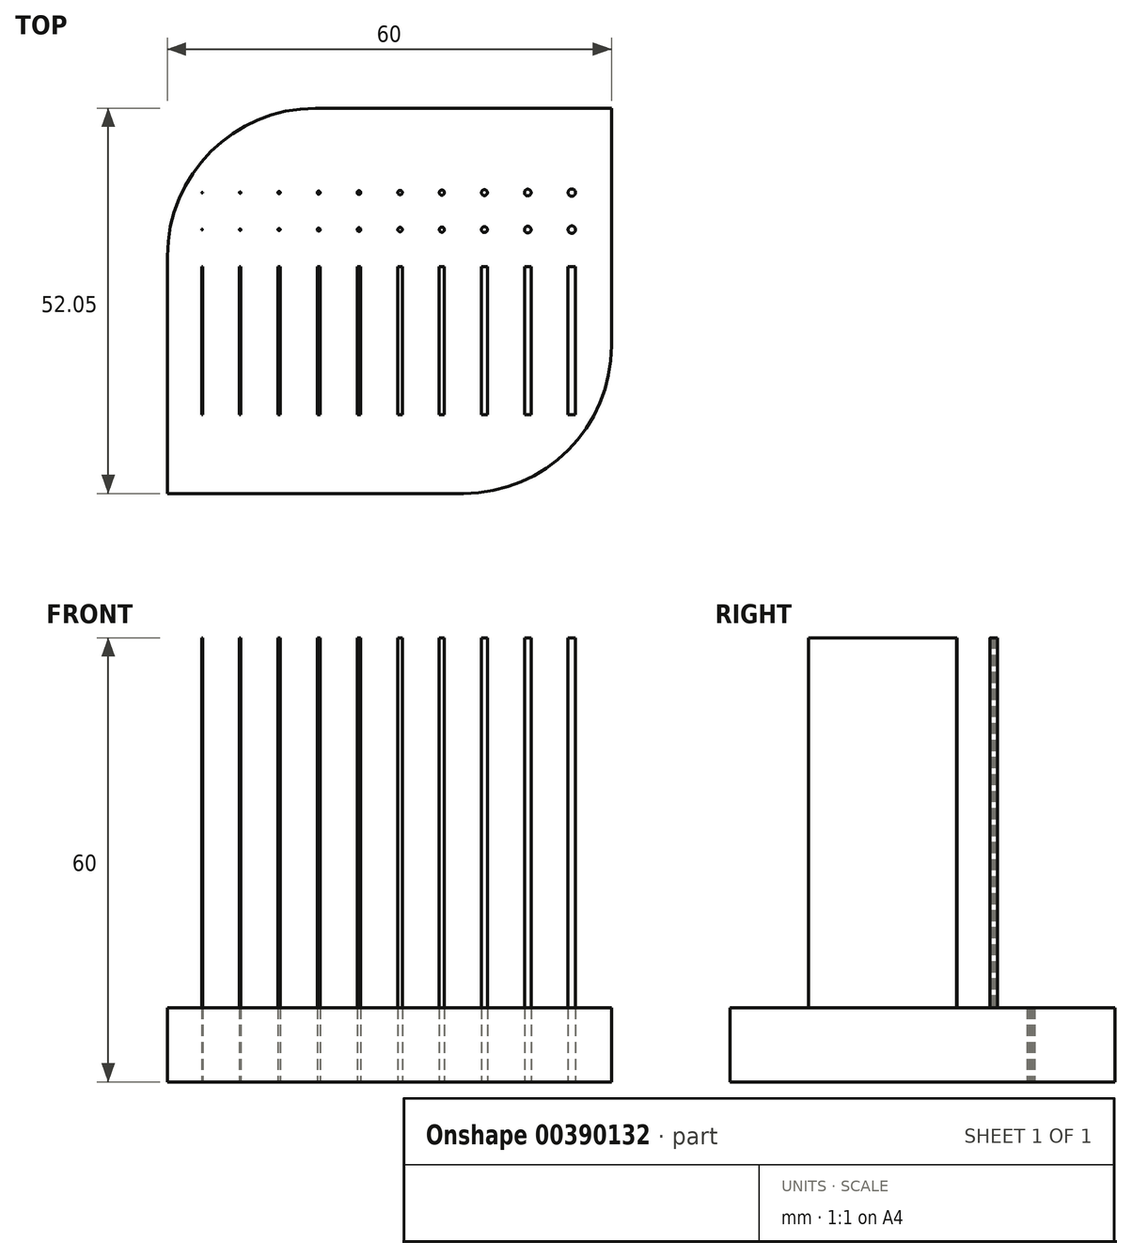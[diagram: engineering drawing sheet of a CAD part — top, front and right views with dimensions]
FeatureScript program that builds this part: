
annotation { "Feature Type Name" : "Feature", "Feature Type Description" : "" }
export const myFeature = defineFeature(function(context is Context, id is Id, definition is map)
    precondition{}
    {
        {
            var Q0;
            Q0=qCreatedBy(makeId("Top.planeOp"),FACE);
            var sketch = newSketch(context, id + "F0", { "sketchPlane" : qUnion([Q0])});
            skLineSegment(sketch, "E0.bottom", {"start": v(-10, 29.74) * mm, "end": v(30, 29.74) * mm});
            skLineSegment(sketch, "E0.top", {"start": v(-30, -22.3) * mm, "end": v(10, -22.3) * mm});
            skLineSegment(sketch, "E0.left", {"start": v(-30, 9.74) * mm, "end": v(-30, -22.3) * mm});
            skLineSegment(sketch, "E0.right", {"start": v(30, 29.74) * mm, "end": v(30, -2.3) * mm});
            skPoint(sketch, "E1.visualSharp", {"position": v(-30, 29.74) * mm});
            skArc(sketch, "E1.filletArc", {"start": v(-10, 29.74) * mm, "mid": v(-24.14, 23.88) * mm, "end": v(-30, 9.74) * mm});
            skPoint(sketch, "E2.visualSharp", {"position": v(30, -22.3) * mm});
            skArc(sketch, "E2.filletArc", {"start": v(10, -22.3) * mm, "mid": v(24.14, -16.45) * mm, "end": v(30, -2.3) * mm});
            skLineSegment(sketch, "E3.bottom", {"start": v(-25.37, 8.34) * mm, "end": v(-25.27, 8.34) * mm});
            skLineSegment(sketch, "E3.top", {"start": v(-25.37, -11.67) * mm, "end": v(-25.27, -11.67) * mm});
            skLineSegment(sketch, "E3.left", {"start": v(-25.37, 8.34) * mm, "end": v(-25.37, -11.67) * mm});
            skLineSegment(sketch, "E3.right", {"start": v(-25.27, 8.34) * mm, "end": v(-25.27, -11.67) * mm});
            skLineSegment(sketch, "E4.bottom", {"start": v(-20.27, 8.33) * mm, "end": v(-20.07, 8.33) * mm});
            skLineSegment(sketch, "E4.top", {"start": v(-20.27, -11.67) * mm, "end": v(-20.07, -11.67) * mm});
            skLineSegment(sketch, "E4.left", {"start": v(-20.27, 8.33) * mm, "end": v(-20.27, -11.67) * mm});
            skLineSegment(sketch, "E4.right", {"start": v(-20.07, 8.33) * mm, "end": v(-20.07, -11.67) * mm});
            skLineSegment(sketch, "E5.bottom", {"start": v(-15.07, 8.33) * mm, "end": v(-14.77, 8.33) * mm});
            skLineSegment(sketch, "E5.top", {"start": v(-15.07, -11.67) * mm, "end": v(-14.77, -11.67) * mm});
            skLineSegment(sketch, "E5.left", {"start": v(-15.07, 8.33) * mm, "end": v(-15.07, -11.67) * mm});
            skLineSegment(sketch, "E5.right", {"start": v(-14.77, 8.33) * mm, "end": v(-14.77, -11.67) * mm});
            skLineSegment(sketch, "E6.bottom", {"start": v(-9.77, 8.33) * mm, "end": v(-9.37, 8.33) * mm});
            skLineSegment(sketch, "E6.top", {"start": v(-9.77, -11.67) * mm, "end": v(-9.37, -11.67) * mm});
            skLineSegment(sketch, "E6.left", {"start": v(-9.77, 8.33) * mm, "end": v(-9.77, -11.67) * mm});
            skLineSegment(sketch, "E6.right", {"start": v(-9.37, 8.33) * mm, "end": v(-9.37, -11.67) * mm});
            skLineSegment(sketch, "E7.bottom", {"start": v(-4.37, 8.33) * mm, "end": v(-3.87, 8.33) * mm});
            skLineSegment(sketch, "E7.top", {"start": v(-4.37, -11.67) * mm, "end": v(-3.87, -11.67) * mm});
            skLineSegment(sketch, "E7.left", {"start": v(-4.37, 8.33) * mm, "end": v(-4.37, -11.67) * mm});
            skLineSegment(sketch, "E7.right", {"start": v(-3.87, 8.33) * mm, "end": v(-3.87, -11.67) * mm});
            skLineSegment(sketch, "E8.bottom", {"start": v(1.13, 8.33) * mm, "end": v(1.73, 8.33) * mm});
            skLineSegment(sketch, "E8.top", {"start": v(1.13, -11.67) * mm, "end": v(1.73, -11.67) * mm});
            skLineSegment(sketch, "E8.left", {"start": v(1.13, 8.33) * mm, "end": v(1.13, -11.67) * mm});
            skLineSegment(sketch, "E8.right", {"start": v(1.73, 8.33) * mm, "end": v(1.73, -11.67) * mm});
            skLineSegment(sketch, "E9.bottom", {"start": v(7.43, 8.33) * mm, "end": v(6.73, 8.33) * mm});
            skLineSegment(sketch, "E9.top", {"start": v(7.43, -11.67) * mm, "end": v(6.73, -11.67) * mm});
            skLineSegment(sketch, "E9.left", {"start": v(7.43, 8.33) * mm, "end": v(7.43, -11.67) * mm});
            skLineSegment(sketch, "E9.right", {"start": v(6.73, 8.33) * mm, "end": v(6.73, -11.67) * mm});
            skLineSegment(sketch, "E10.bottom", {"start": v(13.23, 8.33) * mm, "end": v(12.43, 8.33) * mm});
            skLineSegment(sketch, "E10.top", {"start": v(13.23, -11.67) * mm, "end": v(12.43, -11.67) * mm});
            skLineSegment(sketch, "E10.left", {"start": v(13.23, 8.33) * mm, "end": v(13.23, -11.67) * mm});
            skLineSegment(sketch, "E10.right", {"start": v(12.43, 8.33) * mm, "end": v(12.43, -11.67) * mm});
            skPoint(sketch, "E11.oppositeSnap0", {"position": v(12.83, -11.67) * mm});
            skLineSegment(sketch, "E11.bottom", {"start": v(19.13, 8.33) * mm, "end": v(18.23, 8.33) * mm});
            skLineSegment(sketch, "E11.top", {"start": v(19.13, -11.67) * mm, "end": v(18.23, -11.67) * mm});
            skLineSegment(sketch, "E11.left", {"start": v(19.13, 8.33) * mm, "end": v(19.13, -11.67) * mm});
            skLineSegment(sketch, "E11.right", {"start": v(18.23, 8.33) * mm, "end": v(18.23, -11.67) * mm});
            skLineSegment(sketch, "E12.bottom", {"start": v(24.13, 8.33) * mm, "end": v(25.13, 8.33) * mm});
            skLineSegment(sketch, "E12.top", {"start": v(24.13, -11.67) * mm, "end": v(25.13, -11.67) * mm});
            skLineSegment(sketch, "E12.left", {"start": v(24.13, 8.33) * mm, "end": v(24.13, -11.67) * mm});
            skLineSegment(sketch, "E12.right", {"start": v(25.13, 8.33) * mm, "end": v(25.13, -11.67) * mm});
            skLineSegment(sketch, "E13", {"start": v(-25.37, -11.67) * mm, "end": v(25.13, -11.67) * mm, "construction": true});
            skCircle(sketch, "E14", {"center": v(-25.32, 13.34) * mm, "radius": 0.05 * mm});
            skCircle(sketch, "E15", {"center": v(-20.17, 13.34) * mm, "radius": 0.1 * mm});
            skCircle(sketch, "E16", {"center": v(-14.92, 13.34) * mm, "radius": 0.15 * mm});
            skCircle(sketch, "E17", {"center": v(-9.57, 13.34) * mm, "radius": 0.2 * mm});
            skCircle(sketch, "E18", {"center": v(-4.12, 13.34) * mm, "radius": 0.25 * mm});
            skCircle(sketch, "E19", {"center": v(1.43, 13.34) * mm, "radius": 0.3 * mm});
            skCircle(sketch, "E20", {"center": v(7.08, 13.34) * mm, "radius": 0.35 * mm});
            skCircle(sketch, "E21", {"center": v(12.83, 13.34) * mm, "radius": 0.4 * mm});
            skCircle(sketch, "E22", {"center": v(18.68, 13.34) * mm, "radius": 0.45 * mm});
            skCircle(sketch, "E23", {"center": v(24.63, 13.34) * mm, "radius": 0.5 * mm});
            skLineSegment(sketch, "E24", {"start": v(24.63, 8.33) * mm, "end": v(24.63, 13.34) * mm, "construction": true});
            skLineSegment(sketch, "E25", {"start": v(24.63, 13.34) * mm, "end": v(-25.32, 13.34) * mm, "construction": true});
            skPoint(sketch, "E25.endSnap0", {"position": v(-25.32, 8.34) * mm});
            skLineSegment(sketch, "E26", {"start": v(-25.32, 8.34) * mm, "end": v(-25.32, 13.34) * mm, "construction": true});
            skLineSegment(sketch, "E27", {"start": v(-20.17, 8.33) * mm, "end": v(-20.17, 13.34) * mm, "construction": true});
            skLineSegment(sketch, "E28", {"start": v(-14.92, 8.33) * mm, "end": v(-14.92, 13.34) * mm, "construction": true});
            skLineSegment(sketch, "E29", {"start": v(-9.57, 8.33) * mm, "end": v(-9.57, 13.34) * mm, "construction": true});
            skLineSegment(sketch, "E30", {"start": v(-4.12, 8.33) * mm, "end": v(-4.12, 13.34) * mm, "construction": true});
            skLineSegment(sketch, "E31", {"start": v(1.43, 8.33) * mm, "end": v(1.43, 13.34) * mm, "construction": true});
            skLineSegment(sketch, "E32", {"start": v(7.08, 8.33) * mm, "end": v(7.08, 13.34) * mm, "construction": true});
            skLineSegment(sketch, "E33", {"start": v(12.83, 8.33) * mm, "end": v(12.83, 13.34) * mm, "construction": true});
            skLineSegment(sketch, "E34", {"start": v(18.68, 8.33) * mm, "end": v(18.68, 13.34) * mm, "construction": true});
            skCircle(sketch, "E35", {"center": v(-25.3, 18.34) * mm, "radius": 0.05 * mm});
            skCircle(sketch, "E36", {"center": v(-20.17, 18.34) * mm, "radius": 0.1 * mm});
            skCircle(sketch, "E37", {"center": v(-14.92, 18.34) * mm, "radius": 0.15 * mm});
            skCircle(sketch, "E38", {"center": v(-9.57, 18.34) * mm, "radius": 0.2 * mm});
            skCircle(sketch, "E39", {"center": v(-4.12, 18.34) * mm, "radius": 0.25 * mm});
            skCircle(sketch, "E40", {"center": v(1.43, 18.34) * mm, "radius": 0.3 * mm});
            skCircle(sketch, "E41", {"center": v(7.08, 18.34) * mm, "radius": 0.35 * mm});
            skCircle(sketch, "E42", {"center": v(12.83, 18.34) * mm, "radius": 0.4 * mm});
            skCircle(sketch, "E43", {"center": v(18.68, 18.34) * mm, "radius": 0.45 * mm});
            skCircle(sketch, "E44", {"center": v(24.63, 18.34) * mm, "radius": 0.5 * mm});
            skLineSegment(sketch, "E45", {"start": v(24.63, 18.34) * mm, "end": v(-25.3, 18.34) * mm, "construction": true});
            skLineSegment(sketch, "E46", {"start": v(-25.32, 13.34) * mm, "end": v(-25.3, 18.34) * mm, "construction": true});
            skLineSegment(sketch, "E47", {"start": v(-20.17, 13.34) * mm, "end": v(-20.17, 18.34) * mm, "construction": true});
            skLineSegment(sketch, "E48", {"start": v(-14.92, 13.34) * mm, "end": v(-14.92, 18.34) * mm, "construction": true});
            skLineSegment(sketch, "E49", {"start": v(-9.57, 13.34) * mm, "end": v(-9.57, 18.34) * mm, "construction": true});
            skLineSegment(sketch, "E50", {"start": v(-4.12, 13.34) * mm, "end": v(-4.12, 18.34) * mm, "construction": true});
            skLineSegment(sketch, "E51", {"start": v(1.43, 13.34) * mm, "end": v(1.43, 18.34) * mm, "construction": true});
            skLineSegment(sketch, "E52", {"start": v(7.08, 13.34) * mm, "end": v(7.08, 18.34) * mm, "construction": true});
            skLineSegment(sketch, "E53", {"start": v(12.83, 13.34) * mm, "end": v(12.83, 18.34) * mm, "construction": true});
            skLineSegment(sketch, "E54", {"start": v(18.68, 13.34) * mm, "end": v(18.68, 18.34) * mm, "construction": true});
            skLineSegment(sketch, "E55", {"start": v(24.63, 13.34) * mm, "end": v(24.63, 18.34) * mm, "construction": true});
            skSolve(sketch);
        }
        {
            var Q0;
            Q0=makeQuery(id+"F0.imprint","IMPRINT",FACE,{"disambiguationData":[TD([[makeQuery(id+"F0.imprint","IMPRINT",EDGE,{"derivedFrom":sQuery(id+"F0.wireOp",EDGE,"E10.bottom")}),1.0]])]});
            var Q1;
            Q1=makeQuery(id+"F0.imprint","IMPRINT",FACE,{"disambiguationData":[TD([[makeQuery(id+"F0.imprint","IMPRINT",EDGE,{"derivedFrom":sQuery(id+"F0.wireOp",EDGE,"E11.bottom")}),1.0]])]});
            var Q2;
            Q2=makeQuery(id+"F0.imprint","IMPRINT",FACE,{"disambiguationData":[TD([[makeQuery(id+"F0.imprint","IMPRINT",EDGE,{"derivedFrom":sQuery(id+"F0.wireOp",EDGE,"E12.bottom")}),-1.0]])]});
            var Q3;
            Q3=makeQuery(id+"F0.imprint","IMPRINT",FACE,{"disambiguationData":[TD([[makeQuery(id+"F0.imprint","IMPRINT",EDGE,{"derivedFrom":sQuery(id+"F0.wireOp",EDGE,"E3.bottom")}),-1.0]])]});
            var Q4;
            Q4=makeQuery(id+"F0.imprint","IMPRINT",FACE,{"disambiguationData":[TD([[makeQuery(id+"F0.imprint","IMPRINT",EDGE,{"derivedFrom":sQuery(id+"F0.wireOp",EDGE,"E4.bottom")}),-1.0]])]});
            var Q5;
            Q5=makeQuery(id+"F0.imprint","IMPRINT",FACE,{"disambiguationData":[TD([[makeQuery(id+"F0.imprint","IMPRINT",EDGE,{"derivedFrom":sQuery(id+"F0.wireOp",EDGE,"E5.bottom")}),-1.0]])]});
            var Q6;
            Q6=makeQuery(id+"F0.imprint","IMPRINT",FACE,{"disambiguationData":[TD([[makeQuery(id+"F0.imprint","IMPRINT",EDGE,{"derivedFrom":sQuery(id+"F0.wireOp",EDGE,"E6.bottom")}),-1.0]])]});
            var Q7;
            Q7=makeQuery(id+"F0.imprint","IMPRINT",FACE,{"disambiguationData":[TD([[makeQuery(id+"F0.imprint","IMPRINT",EDGE,{"derivedFrom":sQuery(id+"F0.wireOp",EDGE,"E7.bottom")}),-1.0]])]});
            var Q8;
            Q8=makeQuery(id+"F0.imprint","IMPRINT",FACE,{"disambiguationData":[TD([[makeQuery(id+"F0.imprint","IMPRINT",EDGE,{"derivedFrom":sQuery(id+"F0.wireOp",EDGE,"E8.bottom")}),-1.0]])]});
            var Q9;
            Q9=makeQuery(id+"F0.imprint","IMPRINT",FACE,{"disambiguationData":[TD([[makeQuery(id+"F0.imprint","IMPRINT",EDGE,{"derivedFrom":sQuery(id+"F0.wireOp",EDGE,"E9.bottom")}),1.0]])]});
            var Q10;
            Q10=makeQuery(id+"F0.imprint","IMPRINT",FACE,{"disambiguationData":[TD([[makeQuery(id+"F0.imprint","IMPRINT",EDGE,{"derivedFrom":sQuery(id+"F0.wireOp",EDGE,"E19")}),1.0]])]});
            var Q11;
            Q11=makeQuery(id+"F0.imprint","IMPRINT",FACE,{"disambiguationData":[TD([[makeQuery(id+"F0.imprint","IMPRINT",EDGE,{"derivedFrom":sQuery(id+"F0.wireOp",EDGE,"E17")}),1.0]])]});
            var Q12;
            Q12=makeQuery(id+"F0.imprint","IMPRINT",FACE,{"disambiguationData":[TD([[makeQuery(id+"F0.imprint","IMPRINT",EDGE,{"derivedFrom":sQuery(id+"F0.wireOp",EDGE,"E18")}),1.0]])]});
            var Q13;
            Q13=makeQuery(id+"F0.imprint","IMPRINT",FACE,{"disambiguationData":[TD([[makeQuery(id+"F0.imprint","IMPRINT",EDGE,{"derivedFrom":sQuery(id+"F0.wireOp",EDGE,"E20")}),1.0]])]});
            var Q14;
            Q14=makeQuery(id+"F0.imprint","IMPRINT",FACE,{"disambiguationData":[TD([[makeQuery(id+"F0.imprint","IMPRINT",EDGE,{"derivedFrom":sQuery(id+"F0.wireOp",EDGE,"E15")}),1.0]])]});
            var Q15;
            Q15=makeQuery(id+"F0.imprint","IMPRINT",FACE,{"disambiguationData":[TD([[makeQuery(id+"F0.imprint","IMPRINT",EDGE,{"derivedFrom":sQuery(id+"F0.wireOp",EDGE,"E16")}),1.0]])]});
            var Q16;
            Q16=makeQuery(id+"F0.imprint","IMPRINT",FACE,{"disambiguationData":[TD([[makeQuery(id+"F0.imprint","IMPRINT",EDGE,{"derivedFrom":sQuery(id+"F0.wireOp",EDGE,"E21")}),1.0]])]});
            var Q17;
            Q17=makeQuery(id+"F0.imprint","IMPRINT",FACE,{"disambiguationData":[TD([[makeQuery(id+"F0.imprint","IMPRINT",EDGE,{"derivedFrom":sQuery(id+"F0.wireOp",EDGE,"E22")}),1.0]])]});
            var Q18;
            Q18=makeQuery(id+"F0.imprint","IMPRINT",FACE,{"disambiguationData":[TD([[makeQuery(id+"F0.imprint","IMPRINT",EDGE,{"derivedFrom":sQuery(id+"F0.wireOp",EDGE,"E23")}),1.0]])]});
            var Q19;
            Q19=makeQuery(id+"F0.imprint","IMPRINT",FACE,{"disambiguationData":[TD([[makeQuery(id+"F0.imprint","IMPRINT",EDGE,{"derivedFrom":sQuery(id+"F0.wireOp",EDGE,"E14")}),1.0]])]});
            var Q20;
            Q20=makeQuery(id+"F0.imprint","IMPRINT",FACE,{"disambiguationData":[TD([[makeQuery(id+"F0.imprint","IMPRINT",EDGE,{"derivedFrom":sQuery(id+"F0.wireOp",EDGE,"E0.bottom")}),-1.0]])]});
            extrude(context, id + "F1", {"entities" : qUnion([Q0, Q1, Q2, Q3, Q4, Q5, Q6, Q7, Q8, Q9, Q10, Q11, Q12, Q13, Q14, Q15, Q16, Q17, Q18, Q19, Q20]), "depth" : 10 * mm});
        }
        {
            var Q0;
            Q0=makeQuery(id+"F1.opExtrude","CAP_FACE",FACE,{"disambiguationData":[OSD([sQuery(id+"F0.wireOp",EDGE,"E0.bottom"),sQuery(id+"F0.wireOp",EDGE,"E0.top"),sQuery(id+"F0.wireOp",EDGE,"E0.left"),sQuery(id+"F0.wireOp",EDGE,"E0.right"),sQuery(id+"F0.wireOp",EDGE,"E1.filletArc"),sQuery(id+"F0.wireOp",EDGE,"E2.filletArc"),sQuery(id+"F0.wireOp",EDGE,"E35"),sQuery(id+"F0.wireOp",EDGE,"E36"),sQuery(id+"F0.wireOp",EDGE,"E37"),sQuery(id+"F0.wireOp",EDGE,"E38"),sQuery(id+"F0.wireOp",EDGE,"E39"),sQuery(id+"F0.wireOp",EDGE,"E40"),sQuery(id+"F0.wireOp",EDGE,"E41"),sQuery(id+"F0.wireOp",EDGE,"E42"),sQuery(id+"F0.wireOp",EDGE,"E43"),sQuery(id+"F0.wireOp",EDGE,"E44")])],"isStart":false});
            var sketch = newSketch(context, id + "F2", { "sketchPlane" : qUnion([Q0])});
            skLineSegment(sketch, "E56.0", {"start": v(18.23, 8.33) * mm, "end": v(18.23, -11.67) * mm});
            skLineSegment(sketch, "E56.2", {"start": v(6.73, 8.33) * mm, "end": v(6.73, -11.67) * mm});
            skLineSegment(sketch, "E56.4", {"start": v(-14.77, 8.33) * mm, "end": v(-14.77, -11.67) * mm});
            skLineSegment(sketch, "E56.5", {"start": v(7.43, 8.33) * mm, "end": v(7.43, -11.67) * mm});
            skLineSegment(sketch, "E56.6", {"start": v(-3.87, 8.33) * mm, "end": v(-3.87, -11.67) * mm});
            skLineSegment(sketch, "E56.9", {"start": v(19.13, 8.33) * mm, "end": v(19.13, -11.67) * mm});
            skLineSegment(sketch, "E56.10", {"start": v(-4.37, 8.33) * mm, "end": v(-4.37, -11.67) * mm});
            skLineSegment(sketch, "E56.11", {"start": v(-15.07, 8.33) * mm, "end": v(-15.07, -11.67) * mm});
            skLineSegment(sketch, "E56.12", {"start": v(-20.27, 8.33) * mm, "end": v(-20.27, -11.67) * mm});
            skLineSegment(sketch, "E56.13", {"start": v(-25.27, 8.34) * mm, "end": v(-25.27, -11.67) * mm});
            skLineSegment(sketch, "E56.14", {"start": v(-25.37, 8.34) * mm, "end": v(-25.37, -11.67) * mm});
            skLineSegment(sketch, "E56.15", {"start": v(-20.07, 8.33) * mm, "end": v(-20.07, -11.67) * mm});
            skLineSegment(sketch, "E56.17", {"start": v(12.43, 8.33) * mm, "end": v(12.43, -11.67) * mm});
            skLineSegment(sketch, "E56.20", {"start": v(-9.37, 8.33) * mm, "end": v(-9.37, -11.67) * mm});
            skLineSegment(sketch, "E56.21", {"start": v(1.13, 8.33) * mm, "end": v(1.13, -11.67) * mm});
            skLineSegment(sketch, "E56.23", {"start": v(24.13, 8.33) * mm, "end": v(24.13, -11.67) * mm});
            skLineSegment(sketch, "E56.24", {"start": v(1.73, 8.33) * mm, "end": v(1.73, -11.67) * mm});
            skLineSegment(sketch, "E56.25", {"start": v(13.23, 8.33) * mm, "end": v(13.23, -11.67) * mm});
            skLineSegment(sketch, "E56.26", {"start": v(25.13, 8.33) * mm, "end": v(25.13, -11.67) * mm});
            skLineSegment(sketch, "E56.28", {"start": v(-9.77, 8.33) * mm, "end": v(-9.77, -11.67) * mm});
            skCircle(sketch, "E56.32", {"center": v(-20.17, 13.34) * mm, "radius": 0.1 * mm});
            skCircle(sketch, "E56.33", {"center": v(-14.92, 13.34) * mm, "radius": 0.15 * mm});
            skCircle(sketch, "E56.34", {"center": v(24.63, 13.34) * mm, "radius": 0.5 * mm});
            skCircle(sketch, "E56.35", {"center": v(18.68, 13.34) * mm, "radius": 0.45 * mm});
            skCircle(sketch, "E56.36", {"center": v(1.43, 13.34) * mm, "radius": 0.3 * mm});
            skCircle(sketch, "E56.37", {"center": v(-9.57, 13.34) * mm, "radius": 0.2 * mm});
            skCircle(sketch, "E56.38", {"center": v(-25.32, 13.34) * mm, "radius": 0.05 * mm});
            skCircle(sketch, "E56.39", {"center": v(12.83, 13.34) * mm, "radius": 0.4 * mm});
            skCircle(sketch, "E56.40", {"center": v(7.08, 13.34) * mm, "radius": 0.35 * mm});
            skCircle(sketch, "E56.41", {"center": v(-4.12, 13.34) * mm, "radius": 0.25 * mm});
            skLineSegment(sketch, "E57.0", {"start": v(24.13, 8.33) * mm, "end": v(25.13, 8.33) * mm});
            skLineSegment(sketch, "E58.0", {"start": v(19.13, 8.33) * mm, "end": v(18.23, 8.33) * mm});
            skLineSegment(sketch, "E59.0", {"start": v(13.23, 8.33) * mm, "end": v(12.43, 8.33) * mm});
            skLineSegment(sketch, "E60.0", {"start": v(7.43, 8.33) * mm, "end": v(6.73, 8.33) * mm});
            skLineSegment(sketch, "E61.0", {"start": v(1.13, 8.33) * mm, "end": v(1.73, 8.33) * mm});
            skLineSegment(sketch, "E62.0", {"start": v(-4.37, 8.33) * mm, "end": v(-3.87, 8.33) * mm});
            skLineSegment(sketch, "E63.0", {"start": v(-9.77, 8.33) * mm, "end": v(-9.37, 8.33) * mm});
            skLineSegment(sketch, "E64.0", {"start": v(-15.07, 8.33) * mm, "end": v(-14.77, 8.33) * mm});
            skLineSegment(sketch, "E65.0", {"start": v(-20.27, 8.33) * mm, "end": v(-20.07, 8.33) * mm});
            skLineSegment(sketch, "E66.0", {"start": v(-25.37, 8.34) * mm, "end": v(-25.27, 8.34) * mm});
            skLineSegment(sketch, "E67.0", {"start": v(-20.27, -11.67) * mm, "end": v(-20.07, -11.67) * mm});
            skLineSegment(sketch, "E68", {"start": v(-15.07, -11.67) * mm, "end": v(-14.77, -11.67) * mm});
            skLineSegment(sketch, "E69", {"start": v(-9.77, -11.67) * mm, "end": v(-9.37, -11.67) * mm});
            skLineSegment(sketch, "E70", {"start": v(-4.37, -11.67) * mm, "end": v(-3.87, -11.67) * mm});
            skLineSegment(sketch, "E71", {"start": v(1.13, -11.67) * mm, "end": v(1.73, -11.67) * mm});
            skLineSegment(sketch, "E72", {"start": v(6.73, -11.67) * mm, "end": v(7.43, -11.67) * mm});
            skLineSegment(sketch, "E73", {"start": v(12.43, -11.67) * mm, "end": v(13.23, -11.67) * mm});
            skLineSegment(sketch, "E74", {"start": v(18.23, -11.67) * mm, "end": v(19.13, -11.67) * mm});
            skLineSegment(sketch, "E75", {"start": v(24.13, -11.67) * mm, "end": v(25.13, -11.67) * mm});
            skLineSegment(sketch, "E76", {"start": v(-25.37, -11.67) * mm, "end": v(-25.27, -11.67) * mm});
            skSolve(sketch);
        }
        {
            var Q0;
            Q0=makeQuery(id+"F2.imprint","IMPRINT",FACE,{"disambiguationData":[TD([[makeQuery(id+"F2.imprint","IMPRINT",EDGE,{"derivedFrom":sQuery(id+"F2.wireOp",EDGE,"E56.23")}),1.0]])]});
            var Q1;
            Q1=makeQuery(id+"F2.imprint","IMPRINT",FACE,{"disambiguationData":[TD([[makeQuery(id+"F2.imprint","IMPRINT",EDGE,{"derivedFrom":sQuery(id+"F2.wireOp",EDGE,"E56.12")}),1.0]])]});
            var Q2;
            Q2=makeQuery(id+"F2.imprint","IMPRINT",FACE,{"disambiguationData":[TD([[makeQuery(id+"F2.imprint","IMPRINT",EDGE,{"derivedFrom":sQuery(id+"F2.wireOp",EDGE,"E56.6")}),-1.0]])]});
            var Q3;
            Q3=makeQuery(id+"F2.imprint","IMPRINT",FACE,{"disambiguationData":[TD([[makeQuery(id+"F2.imprint","IMPRINT",EDGE,{"derivedFrom":sQuery(id+"F2.wireOp",EDGE,"E56.0")}),1.0]])]});
            var Q4;
            Q4=makeQuery(id+"F2.imprint","IMPRINT",FACE,{"disambiguationData":[TD([[makeQuery(id+"F2.imprint","IMPRINT",EDGE,{"derivedFrom":sQuery(id+"F2.wireOp",EDGE,"E56.2")}),1.0]])]});
            var Q5;
            Q5=makeQuery(id+"F2.imprint","IMPRINT",FACE,{"disambiguationData":[TD([[makeQuery(id+"F2.imprint","IMPRINT",EDGE,{"derivedFrom":sQuery(id+"F2.wireOp",EDGE,"E56.17")}),1.0]])]});
            var Q6;
            Q6=makeQuery(id+"F2.imprint","IMPRINT",FACE,{"disambiguationData":[TD([[makeQuery(id+"F2.imprint","IMPRINT",EDGE,{"derivedFrom":sQuery(id+"F2.wireOp",EDGE,"E56.21")}),1.0]])]});
            var Q7;
            Q7=makeQuery(id+"F2.imprint","IMPRINT",FACE,{"disambiguationData":[TD([[makeQuery(id+"F2.imprint","IMPRINT",EDGE,{"derivedFrom":sQuery(id+"F2.wireOp",EDGE,"E56.40")}),1.0]])]});
            var Q8;
            Q8=makeQuery(id+"F2.imprint","IMPRINT",FACE,{"disambiguationData":[TD([[makeQuery(id+"F2.imprint","IMPRINT",EDGE,{"derivedFrom":sQuery(id+"F2.wireOp",EDGE,"E56.37")}),1.0]])]});
            var Q9;
            Q9=makeQuery(id+"F2.imprint","IMPRINT",FACE,{"disambiguationData":[TD([[makeQuery(id+"F2.imprint","IMPRINT",EDGE,{"derivedFrom":sQuery(id+"F2.wireOp",EDGE,"E56.33")}),1.0]])]});
            var Q10;
            Q10=makeQuery(id+"F2.imprint","IMPRINT",FACE,{"disambiguationData":[TD([[makeQuery(id+"F2.imprint","IMPRINT",EDGE,{"derivedFrom":sQuery(id+"F2.wireOp",EDGE,"E56.32")}),1.0]])]});
            var Q11;
            Q11=makeQuery(id+"F2.imprint","IMPRINT",FACE,{"disambiguationData":[TD([[makeQuery(id+"F2.imprint","IMPRINT",EDGE,{"derivedFrom":sQuery(id+"F2.wireOp",EDGE,"E56.4")}),-1.0]])]});
            var Q12;
            Q12=makeQuery(id+"F2.imprint","IMPRINT",FACE,{"disambiguationData":[TD([[makeQuery(id+"F2.imprint","IMPRINT",EDGE,{"derivedFrom":sQuery(id+"F2.wireOp",EDGE,"E56.36")}),1.0]])]});
            var Q13;
            Q13=makeQuery(id+"F2.imprint","IMPRINT",FACE,{"disambiguationData":[TD([[makeQuery(id+"F2.imprint","IMPRINT",EDGE,{"derivedFrom":sQuery(id+"F2.wireOp",EDGE,"E56.39")}),1.0]])]});
            var Q14;
            Q14=makeQuery(id+"F2.imprint","IMPRINT",FACE,{"disambiguationData":[TD([[makeQuery(id+"F2.imprint","IMPRINT",EDGE,{"derivedFrom":sQuery(id+"F2.wireOp",EDGE,"E56.38")}),1.0]])]});
            var Q15;
            Q15=makeQuery(id+"F2.imprint","IMPRINT",FACE,{"disambiguationData":[TD([[makeQuery(id+"F2.imprint","IMPRINT",EDGE,{"derivedFrom":sQuery(id+"F2.wireOp",EDGE,"E56.35")}),1.0]])]});
            var Q16;
            Q16=makeQuery(id+"F2.imprint","IMPRINT",FACE,{"disambiguationData":[TD([[makeQuery(id+"F2.imprint","IMPRINT",EDGE,{"derivedFrom":sQuery(id+"F2.wireOp",EDGE,"E56.34")}),1.0]])]});
            var Q17;
            Q17=makeQuery(id+"F2.imprint","IMPRINT",FACE,{"disambiguationData":[TD([[makeQuery(id+"F2.imprint","IMPRINT",EDGE,{"derivedFrom":sQuery(id+"F2.wireOp",EDGE,"E56.41")}),1.0]])]});
            var Q18;
            Q18=makeQuery(id+"F2.imprint","IMPRINT",FACE,{"disambiguationData":[TD([[makeQuery(id+"F2.imprint","IMPRINT",EDGE,{"derivedFrom":sQuery(id+"F2.wireOp",EDGE,"E56.20")}),-1.0]])]});
            var Q19;
            Q19=makeQuery(id+"F2.imprint","IMPRINT",FACE,{"disambiguationData":[TD([[makeQuery(id+"F2.imprint","IMPRINT",EDGE,{"derivedFrom":sQuery(id+"F2.wireOp",EDGE,"E56.13")}),-1.0]])]});
            extrude(context, id + "F3", {"entities" : qUnion([Q0, Q1, Q2, Q3, Q4, Q5, Q6, Q7, Q8, Q9, Q10, Q11, Q12, Q13, Q14, Q15, Q16, Q17, Q18, Q19]), "operationType" : NewBodyOperationType.ADD, "depth" : 50 * mm});
        }
    });
